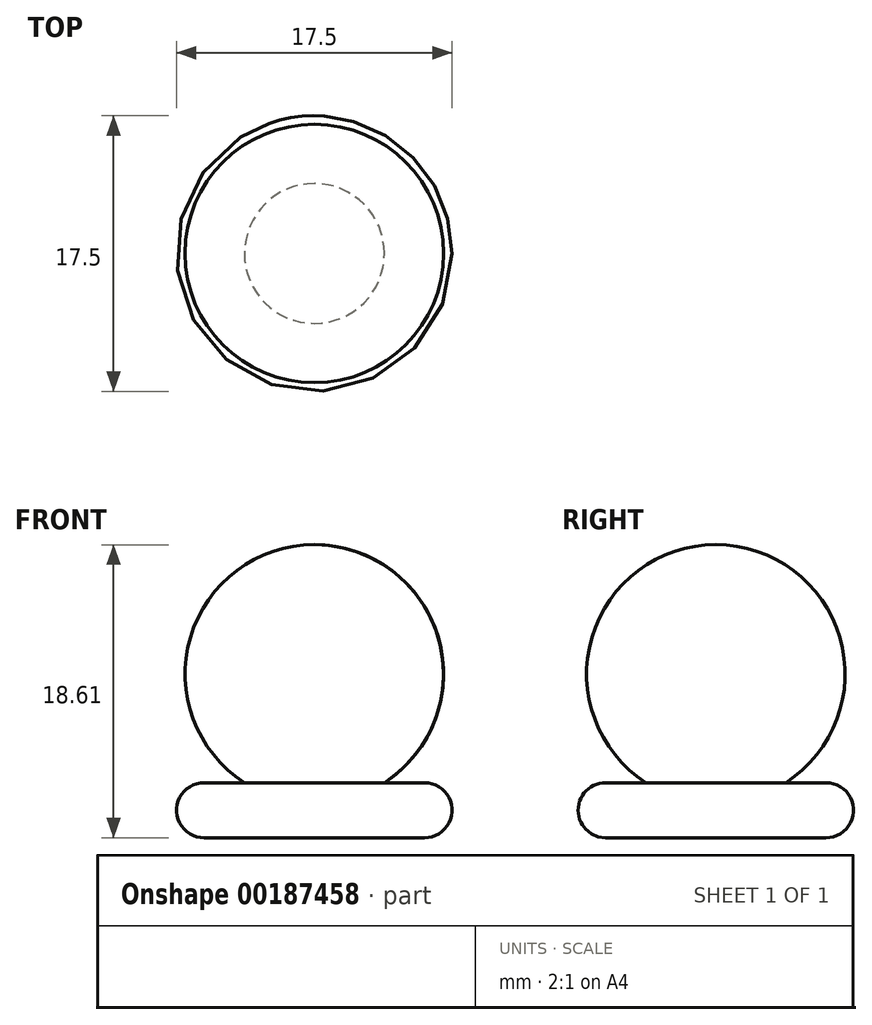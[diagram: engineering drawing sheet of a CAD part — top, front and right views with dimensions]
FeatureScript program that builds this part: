
annotation { "Feature Type Name" : "Feature", "Feature Type Description" : "" }
export const myFeature = defineFeature(function(context is Context, id is Id, definition is map)
    precondition{}
    {
        {
            var Q0;
            Q0=qCreatedBy(makeId("Front.planeOp"),FACE);
            var sketch = newSketch(context, id + "F0", { "sketchPlane" : qUnion([Q0])});
            skLineSegment(sketch, "E0.bottom", {"start": v(0, 0) * mm, "end": v(-7, 0) * mm});
            skLineSegment(sketch, "E0.top", {"start": v(0, 3.5) * mm, "end": v(-7, 3.5) * mm});
            skLineSegment(sketch, "E0.left", {"start": v(0, 0) * mm, "end": v(0, 3.5) * mm});
            skLineSegment(sketch, "E0.right", {"start": v(-7, 0) * mm, "end": v(-7, 3.5) * mm});
            skArc(sketch, "E1", {"start": v(-7, 3.5) * mm, "mid": v(-8.75, 1.75) * mm, "end": v(-7, 0) * mm});
            skLineSegment(sketch, "E2.MirrorCS", {"start": v(0, 3.5) * mm, "end": v(7, 3.5) * mm});
            skLineSegment(sketch, "E3.MirrorCS", {"start": v(0, 0) * mm, "end": v(7, 0) * mm});
            skArc(sketch, "E4.MirrorCS", {"start": v(7, 3.5) * mm, "mid": v(8.75, 1.75) * mm, "end": v(7, 0) * mm});
            skCircle(sketch, "E5", {"center": v(0, 10.4) * mm, "radius": 8.2 * mm});
            skLineSegment(sketch, "E6", {"start": v(0, 18.61) * mm, "end": v(0, 0) * mm});
            skSolve(sketch);
        }
        {
            var Q0;
            {var subQ0=sQuery(id+"F0.wireOp",EDGE,"E6");var subQ3=sQuery(id+"F0.wireOp",EDGE,"E5");var subQ5=makeQuery(id+"F0.imprint","INTERSECT",VERTEX,{"disambiguationData":[OD(0.0)],"derivedFrom":[subQ3,subQ0]});Q0=makeQuery(id+"F0.imprint","IMPRINT",FACE,{"disambiguationData":[TD([[makeQuery(id+"F0.imprint","IMPRINT",EDGE,{"disambiguationData":[TD([[subQ5,-1.0]])],"derivedFrom":subQ3}),1.0]])]});}
            var Q1;
            {var subQ6=sQuery(id+"F0.wireOp",EDGE,"E0.bottom");Q1=makeQuery(id+"F0.imprint","IMPRINT",FACE,{"disambiguationData":[TD([[makeQuery(id+"F0.imprint","IMPRINT",EDGE,{"derivedFrom":subQ6}),-1.0]])]});}
            var Q2;
            Q2=makeQuery(id+"F0.imprint","IMPRINT",FACE,{"disambiguationData":[TD([[makeQuery(id+"F0.imprint","IMPRINT",EDGE,{"derivedFrom":sQuery(id+"F0.wireOp",EDGE,"E0.right")}),1.0]])]});
            var Q3;
            {var subQ1=sQuery(id+"F0.wireOp",EDGE,"E0.top");var subQ3=sQuery(id+"F0.wireOp",EDGE,"E5");var subQ4=makeQuery(id+"F0.imprint","INTERSECT",VERTEX,{"derivedFrom":[subQ1,subQ3]});Q3=makeQuery(id+"F0.imprint","IMPRINT",FACE,{"disambiguationData":[TD([[makeQuery(id+"F0.imprint","IMPRINT",EDGE,{"disambiguationData":[TD([[subQ4,-1.0]])],"derivedFrom":subQ3}),1.0]])]});}
            var Q4;
            Q4=sQuery(id+"F0.wireOp",EDGE,"E6");
            revolve(context, id + "F1", {"entities" : qUnion([Q0, Q1, Q2, Q3]), "axis" : qUnion([Q4]), "revolveType" : RevolveType.FULL});
        }
    });
